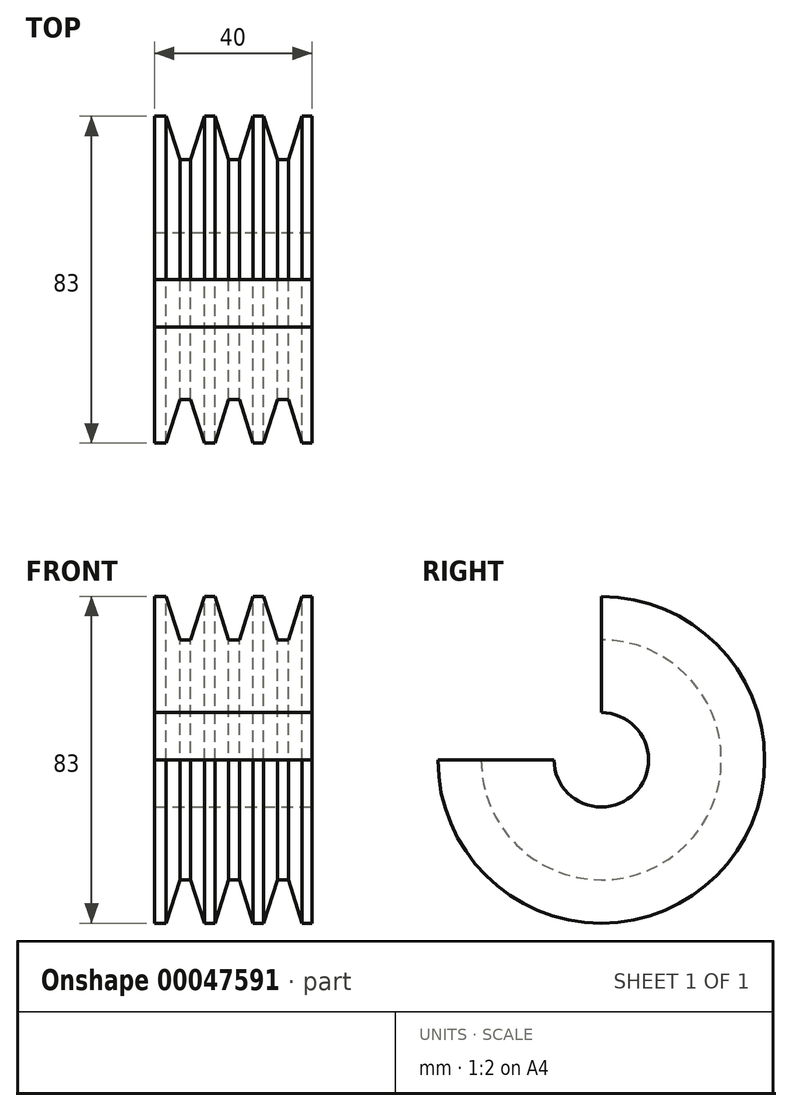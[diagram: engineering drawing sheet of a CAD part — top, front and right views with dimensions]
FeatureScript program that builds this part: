
annotation { "Feature Type Name" : "Feature", "Feature Type Description" : "" }
export const myFeature = defineFeature(function(context is Context, id is Id, definition is map)
    precondition{}
    {
        {
            var Q0;
            Q0=qCreatedBy(makeId("Front.planeOp"),FACE);
            var sketch = newSketch(context, id + "F0", { "sketchPlane" : qUnion([Q0])});
            skLineSegment(sketch, "E0", {"start": v(60.58, 35.91) * mm, "end": v(63.28, 35.91) * mm});
            skLineSegment(sketch, "E1", {"start": v(72.98, 35.91) * mm, "end": v(75.68, 35.91) * mm});
            skLineSegment(sketch, "E2", {"start": v(63.28, 35.91) * mm, "end": v(66.75, 24.91) * mm});
            skLineSegment(sketch, "E3", {"start": v(66.75, 24.91) * mm, "end": v(69.52, 24.91) * mm});
            skLineSegment(sketch, "E4", {"start": v(69.52, 24.91) * mm, "end": v(72.98, 35.91) * mm});
            skLineSegment(sketch, "E5", {"start": v(57.12, 24.91) * mm, "end": v(60.58, 35.91) * mm});
            skLineSegment(sketch, "E6", {"start": v(87.93, 35.91) * mm, "end": v(87.93, -5.59) * mm});
            skLineSegment(sketch, "E7", {"start": v(87.93, -5.59) * mm, "end": v(47.93, -5.59) * mm});
            skLineSegment(sketch, "E8", {"start": v(87.93, 6.41) * mm, "end": v(47.93, 6.41) * mm});
            skLineSegment(sketch, "E9", {"start": v(50.88, 35.91) * mm, "end": v(54.35, 24.91) * mm});
            skLineSegment(sketch, "E10", {"start": v(47.93, 9.71) * mm, "end": v(87.93, 9.71) * mm});
            skLineSegment(sketch, "E11", {"start": v(47.93, 35.91) * mm, "end": v(50.88, 35.91) * mm});
            skLineSegment(sketch, "E12", {"start": v(47.93, -5.59) * mm, "end": v(47.93, 35.91) * mm});
            skLineSegment(sketch, "E13", {"start": v(54.35, 24.91) * mm, "end": v(57.12, 24.91) * mm});
            skLineSegment(sketch, "E14", {"start": v(75.68, 35.91) * mm, "end": v(79.15, 24.91) * mm});
            skLineSegment(sketch, "E15", {"start": v(79.15, 24.91) * mm, "end": v(81.92, 24.91) * mm});
            skLineSegment(sketch, "E16", {"start": v(81.92, 24.91) * mm, "end": v(85.38, 35.91) * mm});
            skLineSegment(sketch, "E17.trimOffspring", {"start": v(85.38, 35.91) * mm, "end": v(87.93, 35.91) * mm});
            skSolve(sketch);
        }
        {
            var Q0;
            Q0=makeQuery(id+"F0.imprint","IMPRINT",FACE,{"disambiguationData":[TD([[makeQuery(id+"F0.imprint","IMPRINT",EDGE,{"derivedFrom":sQuery(id+"F0.wireOp",EDGE,"E0")}),-1.0]])]});
            var Q1;
            {var subQ2=sQuery(id+"F0.wireOp",EDGE,"E8");Q1=makeQuery(id+"F0.imprint","IMPRINT",FACE,{"disambiguationData":[TD([[makeQuery(id+"F0.imprint","IMPRINT",EDGE,{"derivedFrom":subQ2}),-1.0]])]});}
            var Q2;
            Q2=sQuery(id+"F0.wireOp",EDGE,"E7");
            revolve(context, id + "F1", {"entities" : qUnion([Q0, Q1]), "axis" : qUnion([Q2]), "revolveType" : RevolveType.ONE_DIRECTION, "angle" : 270 * degree});
        }
    });
